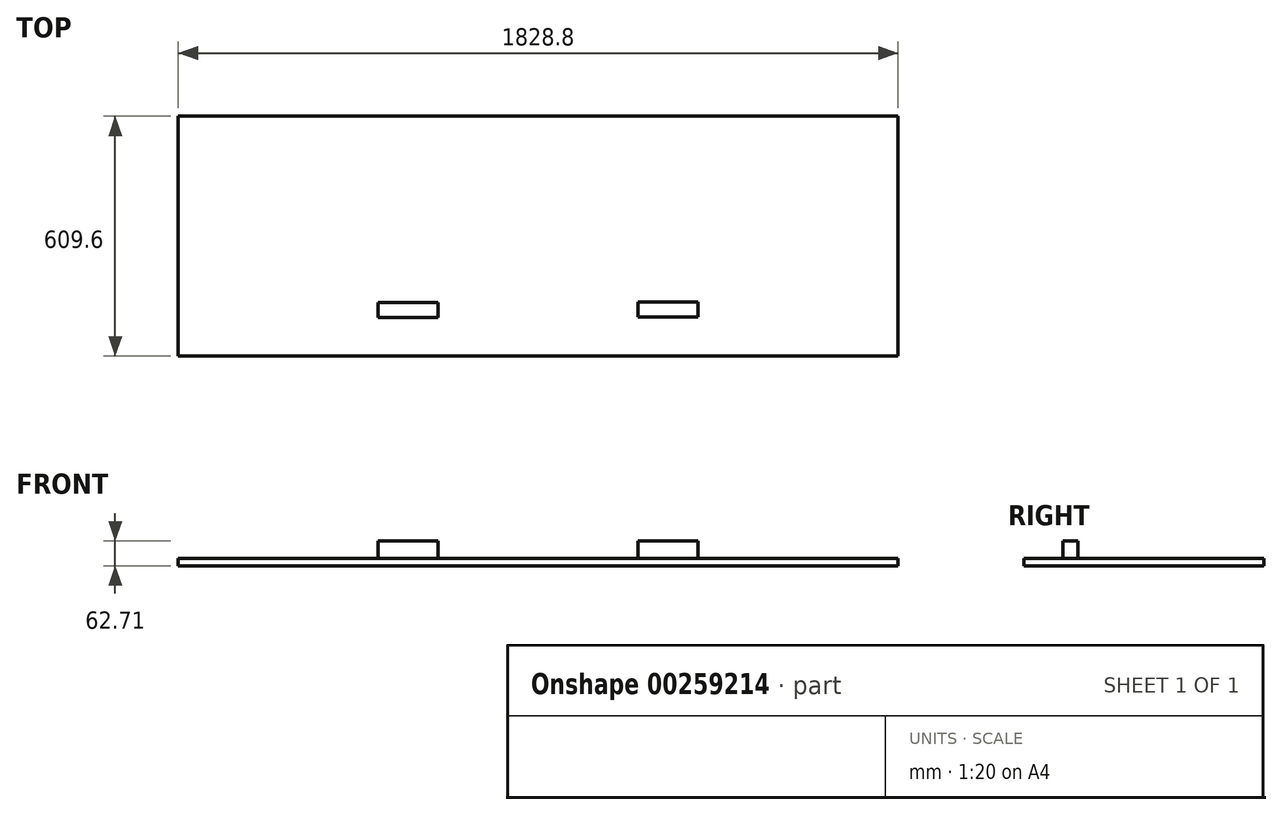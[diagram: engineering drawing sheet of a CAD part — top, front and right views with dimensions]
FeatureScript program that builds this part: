
annotation { "Feature Type Name" : "Feature", "Feature Type Description" : "" }
export const myFeature = defineFeature(function(context is Context, id is Id, definition is map)
    precondition{}
    {
        {
            var Q0;
            Q0=qCreatedBy(makeId("Top.planeOp"),FACE);
            var sketch = newSketch(context, id + "F0", { "sketchPlane" : qUnion([Q0])});
            skLineSegment(sketch, "E0.bottom", {"start": v(0, 0) * mm, "end": v(-1828.8, 0) * mm});
            skLineSegment(sketch, "E0.top", {"start": v(0, 609.6) * mm, "end": v(-1828.8, 609.6) * mm});
            skLineSegment(sketch, "E0.left", {"start": v(0, 0) * mm, "end": v(0, 609.6) * mm});
            skLineSegment(sketch, "E0.right", {"start": v(-1828.8, 0) * mm, "end": v(-1828.8, 609.6) * mm});
            skSolve(sketch);
        }
        {
            var Q0;
            Q0 = qSketchRegion(id + "F0", true);
            extrude(context, id + "F1", {"entities" : qUnion([Q0]), "depth" : 18.26 * mm});
        }
        {
            var Q0;
            Q0=makeQuery(id+"F1.opExtrude","CAP_FACE",FACE,{"disambiguationData":[OSD([sQuery(id+"F0.wireOp",EDGE,"E0.bottom"),sQuery(id+"F0.wireOp",EDGE,"E0.top"),sQuery(id+"F0.wireOp",EDGE,"E0.left"),sQuery(id+"F0.wireOp",EDGE,"E0.right")])],"isStart":false});
            var sketch = newSketch(context, id + "F2", { "sketchPlane" : qUnion([Q0])});
            skLineSegment(sketch, "E1.bottom", {"start": v(-1320.8, 136.66) * mm, "end": v(-1168.4, 136.66) * mm});
            skLineSegment(sketch, "E1.top", {"start": v(-1320.8, 98.56) * mm, "end": v(-1168.4, 98.56) * mm});
            skLineSegment(sketch, "E1.left", {"start": v(-1320.8, 136.66) * mm, "end": v(-1320.8, 98.56) * mm});
            skLineSegment(sketch, "E1.right", {"start": v(-1168.4, 136.66) * mm, "end": v(-1168.4, 98.56) * mm});
            skLineSegment(sketch, "E2.bottom", {"start": v(-660.4, 137.4) * mm, "end": v(-508, 137.4) * mm});
            skLineSegment(sketch, "E2.top", {"start": v(-660.4, 99.3) * mm, "end": v(-508, 99.3) * mm});
            skLineSegment(sketch, "E2.left", {"start": v(-660.4, 137.4) * mm, "end": v(-660.4, 99.3) * mm});
            skLineSegment(sketch, "E2.right", {"start": v(-508, 137.4) * mm, "end": v(-508, 99.3) * mm});
            skLineSegment(sketch, "E3", {"start": v(-1320.8, 117.6) * mm, "end": v(-1828.8, 117.6) * mm, "construction": true});
            skLineSegment(sketch, "E4", {"start": v(-1168.4, 117.6) * mm, "end": v(-660.4, 117.6) * mm, "construction": true});
            skLineSegment(sketch, "E5", {"start": v(-508, 118.35) * mm, "end": v(0, 118.35) * mm, "construction": true});
            skSolve(sketch);
        }
        {
            var Q0;
            Q0=makeQuery(id+"F2.imprint","IMPRINT",FACE,{"disambiguationData":[TD([[makeQuery(id+"F2.imprint","IMPRINT",EDGE,{"derivedFrom":sQuery(id+"F2.wireOp",EDGE,"E1.bottom")}),-1.0]])]});
            var Q1;
            Q1=makeQuery(id+"F2.imprint","IMPRINT",FACE,{"disambiguationData":[TD([[makeQuery(id+"F2.imprint","IMPRINT",EDGE,{"derivedFrom":sQuery(id+"F2.wireOp",EDGE,"E2.bottom")}),-1.0]])]});
            extrude(context, id + "F3", {"entities" : qUnion([Q0, Q1]), "operationType" : NewBodyOperationType.ADD, "depth" : 44.45 * mm});
        }
    });
